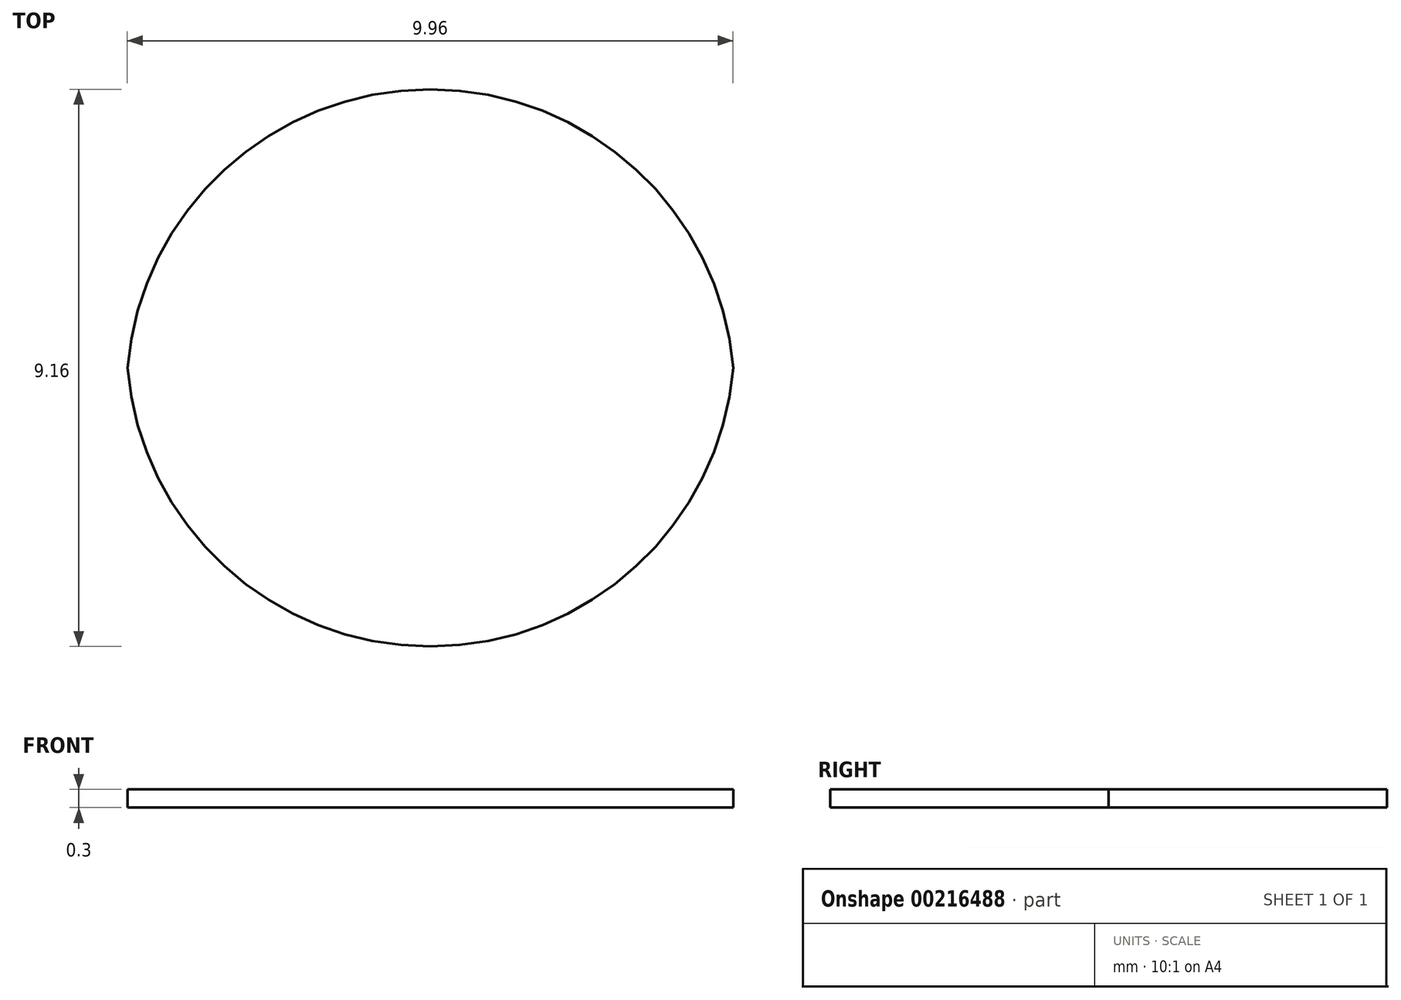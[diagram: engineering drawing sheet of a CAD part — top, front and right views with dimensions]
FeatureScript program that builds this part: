
annotation { "Feature Type Name" : "Feature", "Feature Type Description" : "" }
export const myFeature = defineFeature(function(context is Context, id is Id, definition is map)
    precondition{}
    {
        {
            assignVariable(context, id + "F0", {"name" : "LayerHeight", "anyValue" : 0.3});
        }
        {
            assignVariable(context, id + "F1", {"name" : "NumberOfLayers", "anyValue" : 1});
        }
        {
            var Q0;
            Q0=qCreatedBy(makeId("Top.planeOp"),FACE);
            var sketch = newSketch(context, id + "F2", { "sketchPlane" : qUnion([Q0])});
            skLineSegment(sketch, "E0.bottom", {"start": v(4.6, 4.99) * mm, "end": v(-5.4, 4.99) * mm});
            skLineSegment(sketch, "E0.top", {"start": v(4.6, -4.17) * mm, "end": v(-5.4, -4.17) * mm});
            skLineSegment(sketch, "E0.left", {"start": v(4.6, 4.99) * mm, "end": v(4.6, -4.17) * mm});
            skLineSegment(sketch, "E0.right", {"start": v(-5.4, 4.99) * mm, "end": v(-5.4, -4.17) * mm});
            skPoint(sketch, "E0.middle", {"position": v(-0.4, 0.4) * mm});
            skSolve(sketch);
        }
        {
            var Q0;
            Q0 = qSketchRegion(id + "F2", true);
            extrude(context, id + "F3", {"entities" : qUnion([Q0]), "depth" : (getVariable(context, 'LayerHeight') * getVariable(context, 'NumberOfLayers')) * mm, "offsetDistance" : 25 * mm});
        }
        {
            var Q0;
            Q0=makeQuery(id+"F3.opExtrude","SWEPT_EDGE",EDGE,{"disambiguationData":[OSD([sQuery(id+"F2.wireOp",EDGE,"E0.top"),sQuery(id+"F2.wireOp",EDGE,"E0.left")])]});
            var Q1;
            Q1=makeQuery(id+"F3.opExtrude","SWEPT_EDGE",EDGE,{"disambiguationData":[OSD([sQuery(id+"F2.wireOp",EDGE,"E0.bottom"),sQuery(id+"F2.wireOp",EDGE,"E0.left")])]});
            var Q2;
            Q2=makeQuery(id+"F3.opExtrude","SWEPT_EDGE",EDGE,{"disambiguationData":[OSD([sQuery(id+"F2.wireOp",EDGE,"E0.top"),sQuery(id+"F2.wireOp",EDGE,"E0.right")])]});
            var Q3;
            Q3=makeQuery(id+"F3.opExtrude","SWEPT_EDGE",EDGE,{"disambiguationData":[OSD([sQuery(id+"F2.wireOp",EDGE,"E0.bottom"),sQuery(id+"F2.wireOp",EDGE,"E0.right")])]});
            fillet(context, id + "F4", {"entities" : qUnion([Q0, Q1, Q2, Q3]), "radius" : 5 * mm, "tangentPropagation" : true, "allowEdgeOverflow" : false});
        }
    });
